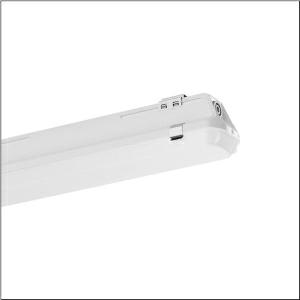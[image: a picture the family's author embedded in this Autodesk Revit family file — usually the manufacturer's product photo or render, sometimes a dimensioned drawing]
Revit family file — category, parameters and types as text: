
# Revit family: monsun_r__21_51fb10mp480b_b142
name_source: partatom
category: Lighting Fixtures
units: mm (PartAtom-declared; Revit-internal decimal feet)

## family parameters
Cut with Voids When Loaded = No
Host = Face
Light Source = No
Part Type = Normal
Room Calculation Point = No
Round Connector Dimension = Use Diameter
Shared = No

## types (1)
- --- (1 x LED, 8190 lm, 53.6 W, 4000K)
    Apparent Load = 54 VA
    CIE Flux Codes = 47 77 93 94 100
    Color Rendering = 80
    Color Temperature = 4000K
    Default Elevation = 1800 mm
    Description = Monsun® 21, damp-proof luminaire, chain hanger, primary optical cover: enclosure, of PMMA, light emission: direct distribution, primary light characteristic: symmetric, installation type: suspended mounting, surface-mounted, horizontal mounting, vertical mounting, LED, rated luminous flux: 8.190lm, luminous efficacy: 153lm/W, light colour: 840, colour temperature: 4000K, control gear: ECG, with terminal, 3-pole, max. 2.5mm², mains connection: 220..240V, AC, 50/60Hz, rated input power: 54W, housing, of glass-fibre reinforced polyester, uncoated, bright grey, incl. chain hanger, length: 1.590mm, width: 90mm, height: 88mm, clip for enclosure, of stainless steel (V2A), ceiling mounting element, of stainless steel (V2A), chain hanger, of stainless steel (V2A), protection rating (complete): IP66, insulation class (complete): insulation class I (protective earthing), certification: CE, ENEC, VDE, UKCA, protection symbol: D, impact resistance: IK04, permissible operating ambient temperature: -25..+35°C, standard: EN 50419, EN 60598-2-1, corresponds to IFS (International Featured Standards) requirements for safety and quality in the food industry, for indoor or canopied outdoor use, no direct snow, no direct sun, no direct rain, contact your sales advisor before using the luminaires in applications with unclear chemical exposure, large temperature fluctuations or condensation-forming humidity, LABS conformity tested according to VDMA 24364:2018-05, packaging unit: 1 piece
    Height = 89 mm
    Lamp = 1 x LED
    Lamp Light Flux = 8190 lm
    Lamp Power = 53.6 W
    Lamp count = 1
    Length = 1590 mm
    Luminous efficacy = 153 lm/W
    Manufacturer = Siteco
    ModVariant = No
    Model = 51FB10MP480B
    Mounting Place = Ceiling
    Mounting Type = Surface mounted
    Number of Poles = 1
    OnlyDefault = Yes
    Power Factor = 1
    Product Name = Monsun® 21
    Product group = damp-proof luminaire
    ProductGroupID = 300
    Protection Class = Protection class I
    Protection Degree = IP 66
    RLX_Detail_Level = 1
    RLX_Emergency_Light_Flux = 0 lm
    RLX_Emergency_Type = 0
    RLX_Emergency_Type_DB = No
    RlxData = <blob elided: 89789 chars, md5=1b03193c>
    Socket = socket
    Standby Power = 0 W
    System Light Flux = 8190 lm
    System Power = 54 W
    Type Comments = factory setting: luminous flux: 100 % | (A | C | E) | 121 mA
    Type Image = l_1006717.jpg
    URL = http://relux.com
    VarID = @adj_079309
    Voltage = 0 V
    Weight = 0.00 kg
    Width = 90 mm

## geometry (parser evidence)
native form markers: Blend x4, Sweep x13
no freeform markers — native parametric forms only
